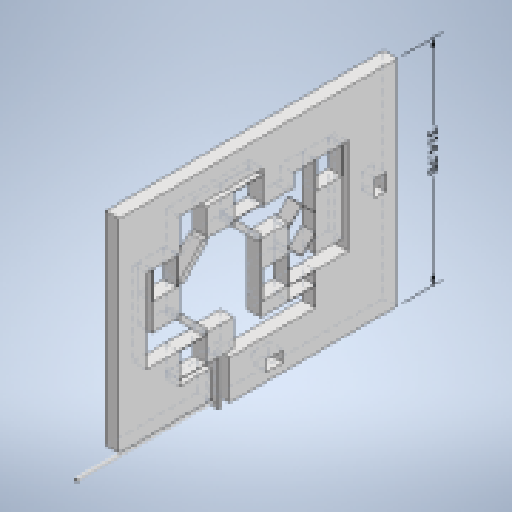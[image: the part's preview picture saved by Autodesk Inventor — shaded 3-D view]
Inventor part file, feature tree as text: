
AUTODESK INVENTOR PART (.ipt)
format: ipt  version: 2023 (Build 270158000, 158)  size: 802,816 bytes
history: native  units: mm
features: sketch x20, extrude x19, other x4, direct_edit x1, projected_geometry x1
ambient origin geometry x8: Origin, YZ Plane, XZ Plane, XY Plane, X Axis, Y Axis, Z Axis, Center Point
bodies: Solide1 (feature_tree)
feature tree (45):
  other  "<userpath>\OneDrive\ClawdDrive\Objet3D\IminaProbe\Settings_CAD.xlsx"
  other  "Annotations"
  extrude  "Extrusion1"  Depth=75.0mm
  extrude  "Extrusion2"  Depth=50.0mm
  extrude  "Extrusion3"  Depth=25.0mm
  sketch  "Sketch4"  dims[d0=75.0mm d1=75.0mm]
  extrude  "Extrusion4"  Depth=10.0mm
  extrude  "Extrusion5"  Depth=40.0mm TaperAngle=360.0deg
  extrude  "Extrusion6"  Depth=1.0mm
  extrude  "Extrusion7"  Depth=1.0mm
  extrude  "Extrusion8"  Depth=0.8mm
  extrude  "Extrusion9"  TaperAngle=45.0deg  [1 undecoded]
  extrude  "Extrusion10"  Depth=1.0mm
  extrude  "Extrusion11"  Depth=0.8mm
  extrude  "Extrusion12"  Depth=0.8mm
  extrude  "Extrusion13"  TaperAngle=45.0deg  [1 undecoded]
  extrude  "Extrusion14"  Depth=1.0mm
  direct_edit  "Direct Edit1"
  extrude  "Extrusion15"  Depth=0.8mm
  extrude  "Extrusion16"  Depth=0.125mm
  extrude  "Extrusion17"  Depth=314.776595mm
  extrude  "Extrusion18"  Depth=314.776595mm
  extrude  "Extrusion19"  Depth=10.0mm
  sketch  "Esquisse1"
  sketch  "Esquisse2"
  sketch  "Esquisse3"
  sketch  "Sketch5"  dims[d2=50.0mm d3=50.0mm]
  sketch  "Sketch6"  dims[d4=5.0mm d5=0.0mm d6=25.0mm]
  sketch  "Sketch7"  dims[d7=10.0mm d8=10.0mm]
  sketch  "Sketch8"  dims[d9=5.0mm d10=40.0mm d12=360.0deg]
  sketch  "Sketch9"  dims[d14=45.0deg d15=1.0mm]
  sketch  "Sketch10"  dims[d16=1.0mm d17=0.8mm]
  sketch  "Sketch11"  dims[d18=0.8mm d19=0.8mm]
  sketch  "Sketch12"  dims[d20=0.8mm d21=45.0deg]
  projected_geometry  "Projected Loop1"
  sketch  "Sketch13"  dims[d22=1.0mm d23=1.0mm]
  sketch  "Sketch14"  dims[d24=0.8mm d25=0.8mm]
  sketch  "Sketch15"  dims[d26=0.8mm d27=0.8mm]
  sketch  "Sketch16"  dims[d28=1.0mm d29=45.0deg]
  sketch  "Sketch17"  dims[d30=1.0mm d31=0.8mm]
  sketch  "Sketch18"  dims[d32=0.8mm d33=0.8mm]
  sketch  "Sketch19"  dims[d34=0.8mm d35=0.125mm]
  sketch  "Sketch21"  dims[d36=10.0mm d37=0.25mm d38=0.125mm d39=10.0mm d40=0.125mm d41=10.0mm d42=0.125mm d43=0.125mm d44=10.0mm d45=0.125mm d46=0.125mm d47=2.0mm d48=2.0mm d49=2.0mm d50=2.0mm d51=5.0mm d52=0.0mm d53=5.0mm d54=0.0mm d55=0.25mm d56=0.25mm d57=0.25mm d58=0.25mm d59=3.0mm d60=3.0mm d61=10.0mm d62=10.0mm d65=135.0deg d66=135.0deg d67=10.0mm d68=10.0mm d71=3.353553mm d72=3.353553mm d73=20.0mm d74=10.0mm d75=10.0mm d76=10.0mm d77=4.0mm d78=3.0mm d79=6.0mm d80=3.0mm d82=5.0mm d83=0.25mm d84=0.353553mm d85=0.25mm d86=0.25mm d87=0.25mm d88=10.0mm d89=10.0mm d90=10.0mm d91=10.0mm d92=10.0mm d93=0.0mm d94=5.0mm d95=0.0mm d97=2.0mm d99=10.0mm d102=4.0mm d103=10.0mm d104=10.0mm d105=0.25mm d106=0.25mm d107=10.0mm d108=5.0mm d109=6.0mm d110=5.0mm d111=0.25mm d112=0.25mm d113=5.0mm d114=5.0mm d115=20.0mm d116=7.0mm d117=6.0mm d118=3.0mm d119=5.0mm d120=0.0mm d121=5.0mm d122=5.0mm d123=3.0mm d124=6.0mm d125=4.0mm d126=20.0mm d127=7.0mm d128=10.0mm d129=0.0mm d130=10.0mm d131=3.0mm d132=3.0mm d133=1.0mm d134=20.0mm d135=5.0mm d136=0.0mm d137=3.0mm d138=5.0mm d139=0.0mm d140=0.5mm d141=5.0mm d142=0.0mm d143=5.0mm d144=0.0mm d145=5.0mm d146=0.0mm d147=10.0mm d148=0.0mm d149=10.0mm d150=0.0mm d154=40.0mm d155=10.0mm d156=10.0mm d157=20.0mm d158=20.0mm d159=20.0mm d160=0.0mm d161=1.0mm d162=1.0mm d163=30.0mm d164=0.0mm d165=30.0mm d166=0.0mm d167=40.0mm d168=20.0mm d169=0.0mm d170=5.0mm d171=10.0mm d172=5.0mm d173=200.0mm d174=0.0mm d175=0.25mm d176=0.25mm d151=2.835368mm d152=0.623298mm d153=314.776595mm]
  other  "Scale1"
  other  "Linear Dimension 1"
note: 2 required parameter values undecoded (feature->parameter linkage not recoverable at this tier; creation-order binding heuristic only, values carry confidence <= 0.55)
